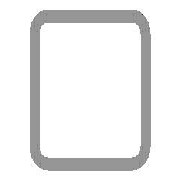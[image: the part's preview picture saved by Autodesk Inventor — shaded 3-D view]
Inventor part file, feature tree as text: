
AUTODESK INVENTOR PART (.ipt)
format: ipt  version: 2025 (Build 290162010, 162A)  size: 133,632 bytes
history: native  units: mm (DEFAULTED — no unit token found)
features: other x4, sketch x1, plane x1
ambient origin geometry x8: Origin, YZ Plane, XZ Plane, XY Plane, X Axis, Y Axis, Z Axis, Center Point
bodies: Solid1 (feature_tree), Body (feature_tree)
feature tree (6):
  parser-record x1  (decoder bookkeeping rows leaked as tree rows — omitted from the tree; the rows remain in map.json)
  other  "Driven Length"
  other  "Start Plane"
  other  "End Plane"
  sketch  "Sketch3"  dims[d3=2120.0mm d4=0.0mm d7=4.0mm d9=40.0mm d11=40.0mm d12=2.0mm d13=-0.0mm d14=2120.0mm d15=20.0mm d16=20.0mm d17=90.0deg d18=2120.0mm]
  plane  "Work Plane3"
